# Revit family: Access_Panel-Wall_Ceiling_Door-Activar-Interior_Access-TMW
name_source: partatom
category: Doors
revit_build: Autodesk Revit MEP 2012 (Build: 20110309_2315(x64)
units: mm (PartAtom-declared; Revit-internal decimal feet)

## types (9) — shared parameters
04 CSI = 08 31 16
95 CSI = 08310
Additional Info URL = http://www.activarcpg.com
Assembly Code = C1020700
Color Availability = Red (R), Black (BK), Flat Black (FB), Sand (S), AMS Beige (AB), SC Flat Beige (SB), Gray (G), Bronze (B), Silver (SI)
Custom Size Note = Custom sizes are available.  Contact manufacturer for availability.
Default Elevation = 48"
Description = Concealed Frame Flush Access Panels for Drywall
Door = 16 gauge steel with concealed continuous hinge.
Drywall Bead Installation = Yes
Frame = 16 gauge with 1" drywall bead that can be taped and mudded.
Hardware = Flush screwdriver-operated cam (C).
Installation URL = http://www.activarcpg.com
Maitenance URL = http://www.activarcpg.com
Manufacturer = Activar Construction Products Group
Manufacturer Fax = 952-835-2218
Options = Cylinder Lock,Mortise Cam Latch, Mortise Deadbolt Lock, Mortise Slam Latch,  Knob Cam, Torx, Spanner or Hex Head Cam, Additional Colors, Plexiglass View Window, Removeable Door (no hinge).
Panel Type Use = Wallboard Bead (Wall or Ceiling)
Product Line = Concealed Frame Access Panels
Product Page URL = http://www.activarcpg.com
Subcategory = Access Panels
Submittal URL = http://www.activarcpg.com
URL = http://www.activarcpg.com
Warranty URL = http://www.activarcpg.com
ecoScorecard Product Page = http://ecoscorecard.com

## per-type parameters (varying)
| type | Height | Model | Number of Latches | Rough Height | Rough Width | Shipping Weight | Width |
| Drywall Installation, 8 x 8 | 10" | TMW-0808CW | 1 | 8 1/2" | 8 1/2" | 4.00 lb | 10" |
| Drywall Installation, 10 x 10 | 12" | TMW-1010CW | 1 | 10 1/2" | 10 1/2" | 5.00 lb | 12" |
| Drywall Installation, 12 x 12 | 14" | TMW-1212CW | 1 | 12 1/2" | 12 1/2" | 7.00 lb | 14" |
| Drywall Installation, 14 x 14 | 16" | TMW-1414CW | 1 | 14 1/2" | 14 1/2" | 8.00 lb | 16" |
| Drywall Installation, 16 x 16 | 18" | TMW-1616CW | 1 | 16 1/2" | 16 1/2" | 10.00 lb | 18" |
| Drywall Installation, 18 x 18 | 20" | TMW-1818CW | 3 | 18 1/2" | 18 1/2" | 12.00 lb | 20" |
| Drywall Installation, 22 x 22 | 24" | TMW-2222CW | 4 | 22 1/2" | 22 1/2" | 16.00 lb | 24" |
| Drywall Installation, 22 x 30 | 32" | TMW-2230CW | 4 | 30 1/2" | 22 1/2" | 21.00 lb | 24" |
| Drywall Installation, 24 x 24 | 26" | TMW-2424CW | 4 | 24 1/2" | 24 1/2" | 19.00 lb | 26" |

## geometry (parser evidence)
native form markers: Blend x4, Sweep x2
no freeform markers — native parametric forms only
